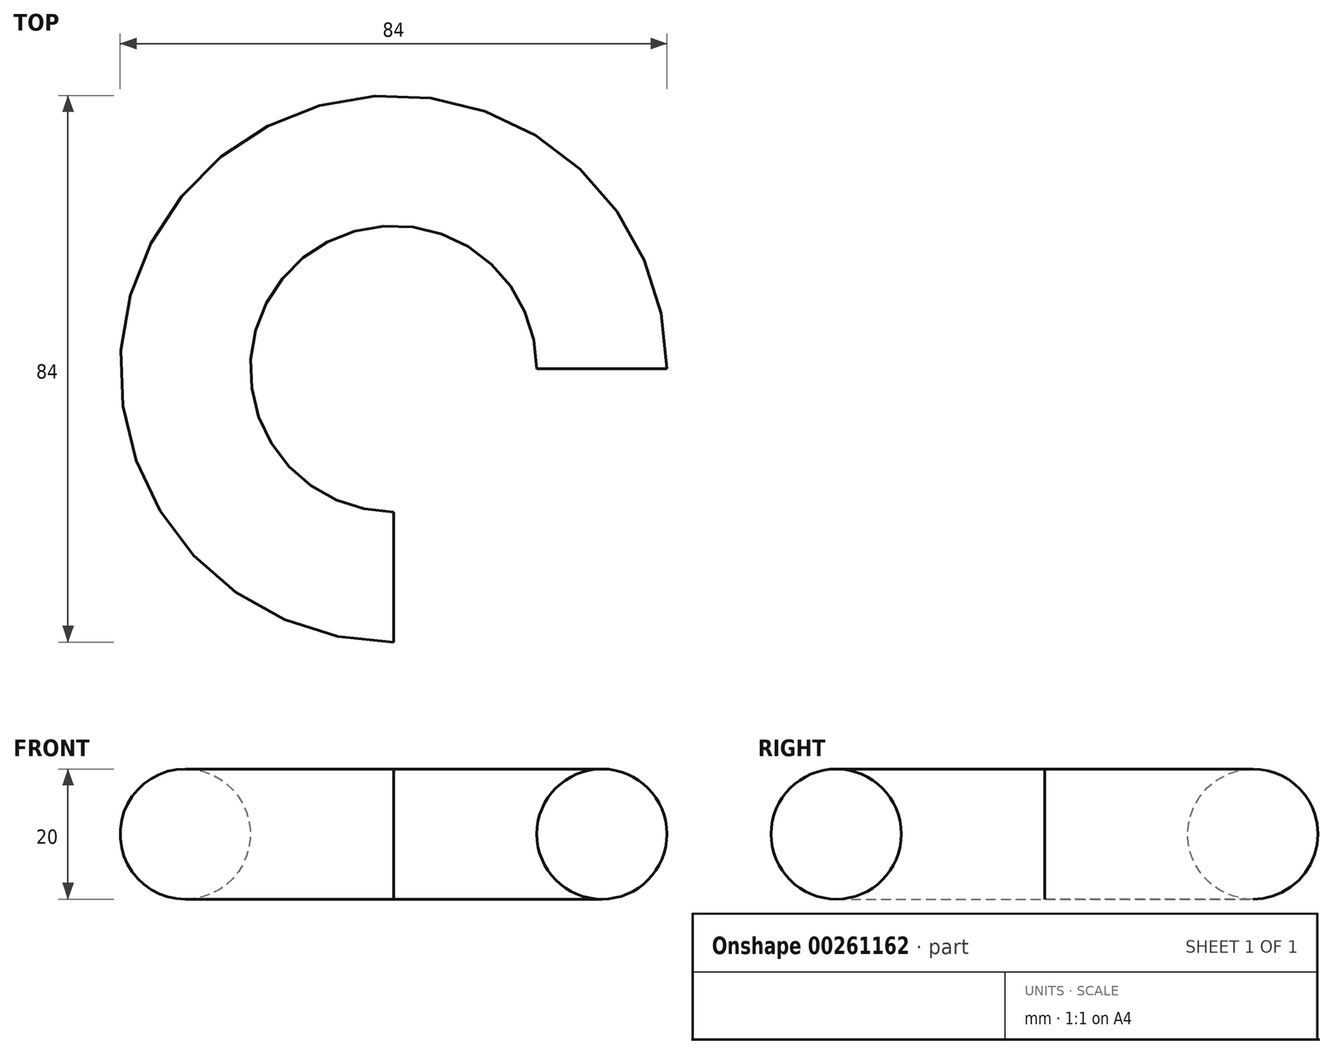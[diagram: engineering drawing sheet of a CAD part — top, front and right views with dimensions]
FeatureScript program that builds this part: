
annotation { "Feature Type Name" : "Feature", "Feature Type Description" : "" }
export const myFeature = defineFeature(function(context is Context, id is Id, definition is map)
    precondition{}
    {
        {
            var Q0;
            Q0=qCreatedBy(makeId("Front.planeOp"),FACE);
            var sketch = newSketch(context, id + "F0", { "sketchPlane" : qUnion([Q0])});
            skCircle(sketch, "E0", {"center": v(32, 0) * mm, "radius": 10 * mm});
            skLineSegment(sketch, "E1", {"start": v(0, 38.64) * mm, "end": v(0, -55.38) * mm});
            skLineSegment(sketch, "E2", {"start": v(0, 38.64) * mm, "end": v(0, -55.38) * mm, "construction": true});
            skSolve(sketch);
        }
        {
            var Q0;
            Q0=makeQuery(id+"F0.imprint","IMPRINT",FACE,{"disambiguationData":[TD([[makeQuery(id+"F0.imprint","IMPRINT",EDGE,{"derivedFrom":sQuery(id+"F0.wireOp",EDGE,"E0")}),1.0]])]});
            var Q1;
            Q1=sQuery(id+"F0.wireOp",EDGE,"E1");
            revolve(context, id + "F1", {"entities" : qUnion([Q0]), "axis" : qUnion([Q1]), "revolveType" : RevolveType.ONE_DIRECTION, "oppositeDirection" : true, "angle" : 270 * degree});
        }
    });
